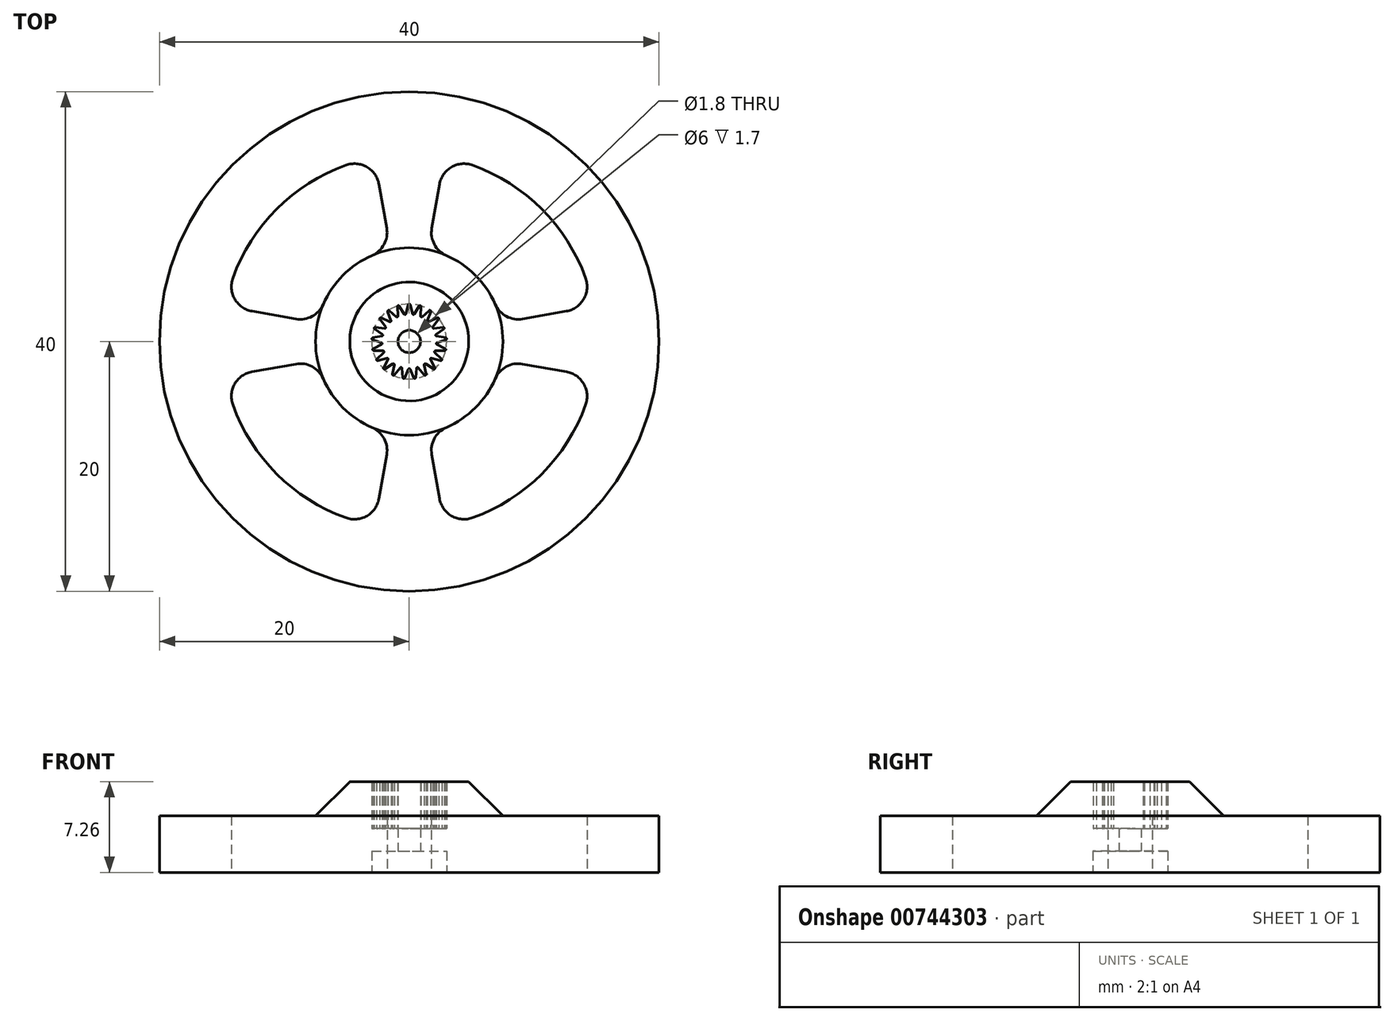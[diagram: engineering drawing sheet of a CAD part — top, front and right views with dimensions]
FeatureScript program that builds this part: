
annotation { "Feature Type Name" : "Feature", "Feature Type Description" : "" }
export const myFeature = defineFeature(function(context is Context, id is Id, definition is map)
    precondition{}
    {
        {
            var Q0;
            Q0=qCreatedBy(makeId("Top.planeOp"),FACE);
            var sketch = newSketch(context, id + "F0", { "sketchPlane" : qUnion([Q0])});
            skCircle(sketch, "E0", {"center": v(0, 0) * mm, "radius": 2.05 * mm, "construction": true});
            skLineSegment(sketch, "E1", {"start": v(-0.26, 2.21) * mm, "end": v(-0.08, 2.94) * mm});
            skLineSegment(sketch, "E2", {"start": v(0.26, 2.21) * mm, "end": v(0.08, 2.94) * mm});
            skArc(sketch, "E3", {"start": v(0.08, 2.94) * mm, "mid": v(0, 3) * mm, "end": v(-0.08, 2.94) * mm});
            skLineSegment(sketch, "E4", {"start": v(-0.3, 2.03) * mm, "end": v(0, 0) * mm, "construction": true});
            skLineSegment(sketch, "E5", {"start": v(0.3, 2.03) * mm, "end": v(0, 0) * mm, "construction": true});
            skLineSegment(sketch, "E6.1.0", {"start": v(-0.9, 2.04) * mm, "end": v(-0.94, 2.79) * mm});
            skArc(sketch, "E6.1.1", {"start": v(-0.8, 2.83) * mm, "mid": v(-0.88, 2.87) * mm, "end": v(-0.94, 2.79) * mm});
            skLineSegment(sketch, "E6.1.2", {"start": v(-0.4, 2.2) * mm, "end": v(-0.8, 2.83) * mm});
            skLineSegment(sketch, "E6.2.0", {"start": v(-1.46, 1.68) * mm, "end": v(-1.72, 2.38) * mm});
            skArc(sketch, "E6.2.1", {"start": v(-1.6, 2.47) * mm, "mid": v(-1.69, 2.48) * mm, "end": v(-1.72, 2.38) * mm});
            skLineSegment(sketch, "E6.2.2", {"start": v(-1.03, 1.97) * mm, "end": v(-1.6, 2.47) * mm});
            skLineSegment(sketch, "E6.3.0", {"start": v(-1.9, 1.18) * mm, "end": v(-2.35, 1.77) * mm});
            skArc(sketch, "E6.3.1", {"start": v(-2.25, 1.9) * mm, "mid": v(-2.35, 1.87) * mm, "end": v(-2.35, 1.77) * mm});
            skLineSegment(sketch, "E6.3.2", {"start": v(-1.57, 1.58) * mm, "end": v(-2.25, 1.9) * mm});
            skLineSegment(sketch, "E6.4.0", {"start": v(-2.16, 0.57) * mm, "end": v(-2.76, 1) * mm});
            skArc(sketch, "E6.4.1", {"start": v(-2.7, 1.15) * mm, "mid": v(-2.8, 1.1) * mm, "end": v(-2.76, 1) * mm});
            skLineSegment(sketch, "E6.4.2", {"start": v(-1.97, 1.05) * mm, "end": v(-2.7, 1.15) * mm});
            skLineSegment(sketch, "E6.5.0", {"start": v(-2.23, -0.1) * mm, "end": v(-2.94, 0.14) * mm});
            skArc(sketch, "E6.5.1", {"start": v(-2.93, 0.3) * mm, "mid": v(-3, 0.22) * mm, "end": v(-2.94, 0.14) * mm});
            skLineSegment(sketch, "E6.5.2", {"start": v(-2.19, 0.42) * mm, "end": v(-2.93, 0.3) * mm});
            skLineSegment(sketch, "E6.6.0", {"start": v(-2.1, -0.75) * mm, "end": v(-2.85, -0.73) * mm});
            skArc(sketch, "E6.6.1", {"start": v(-2.88, -0.58) * mm, "mid": v(-2.92, -0.67) * mm, "end": v(-2.85, -0.73) * mm});
            skLineSegment(sketch, "E6.6.2", {"start": v(-2.22, -0.24) * mm, "end": v(-2.88, -0.58) * mm});
            skLineSegment(sketch, "E6.7.0", {"start": v(-1.79, -1.33) * mm, "end": v(-2.5, -1.54) * mm});
            skArc(sketch, "E6.7.1", {"start": v(-2.58, -1.4) * mm, "mid": v(-2.6, -1.5) * mm, "end": v(-2.5, -1.54) * mm});
            skLineSegment(sketch, "E6.7.2", {"start": v(-2.05, -0.88) * mm, "end": v(-2.58, -1.4) * mm});
            skLineSegment(sketch, "E6.8.0", {"start": v(-1.32, -1.8) * mm, "end": v(-1.94, -2.2) * mm});
            skArc(sketch, "E6.8.1", {"start": v(-2.06, -2.1) * mm, "mid": v(-2.04, -2.2) * mm, "end": v(-1.94, -2.2) * mm});
            skLineSegment(sketch, "E6.8.2", {"start": v(-1.7, -1.45) * mm, "end": v(-2.06, -2.1) * mm});
            skLineSegment(sketch, "E6.9.0", {"start": v(-0.73, -2.1) * mm, "end": v(-1.2, -2.68) * mm});
            skArc(sketch, "E6.9.1", {"start": v(-1.35, -2.61) * mm, "mid": v(-1.3, -2.7) * mm, "end": v(-1.2, -2.68) * mm});
            skLineSegment(sketch, "E6.9.2", {"start": v(-1.2, -1.88) * mm, "end": v(-1.35, -2.61) * mm});
            skLineSegment(sketch, "E6.10.0", {"start": v(-0.07, -2.23) * mm, "end": v(-0.36, -2.92) * mm});
            skArc(sketch, "E6.10.1", {"start": v(-0.51, -2.9) * mm, "mid": v(-0.45, -2.97) * mm, "end": v(-0.36, -2.92) * mm});
            skLineSegment(sketch, "E6.10.2", {"start": v(-0.59, -2.15) * mm, "end": v(-0.51, -2.9) * mm});
            skLineSegment(sketch, "E6.11.0", {"start": v(0.59, -2.15) * mm, "end": v(0.51, -2.9) * mm});
            skArc(sketch, "E6.11.1", {"start": v(0.36, -2.92) * mm, "mid": v(0.45, -2.97) * mm, "end": v(0.51, -2.9) * mm});
            skLineSegment(sketch, "E6.11.2", {"start": v(0.07, -2.23) * mm, "end": v(0.36, -2.92) * mm});
            skLineSegment(sketch, "E6.12.0", {"start": v(1.2, -1.88) * mm, "end": v(1.35, -2.61) * mm});
            skArc(sketch, "E6.12.1", {"start": v(1.2, -2.68) * mm, "mid": v(1.3, -2.7) * mm, "end": v(1.35, -2.61) * mm});
            skLineSegment(sketch, "E6.12.2", {"start": v(0.73, -2.1) * mm, "end": v(1.2, -2.68) * mm});
            skLineSegment(sketch, "E6.13.0", {"start": v(1.7, -1.45) * mm, "end": v(2.06, -2.1) * mm});
            skArc(sketch, "E6.13.1", {"start": v(1.94, -2.2) * mm, "mid": v(2.04, -2.2) * mm, "end": v(2.06, -2.1) * mm});
            skLineSegment(sketch, "E6.13.2", {"start": v(1.32, -1.8) * mm, "end": v(1.94, -2.2) * mm});
            skLineSegment(sketch, "E6.14.0", {"start": v(2.05, -0.88) * mm, "end": v(2.58, -1.4) * mm});
            skArc(sketch, "E6.14.1", {"start": v(2.5, -1.54) * mm, "mid": v(2.6, -1.5) * mm, "end": v(2.58, -1.4) * mm});
            skLineSegment(sketch, "E6.14.2", {"start": v(1.79, -1.33) * mm, "end": v(2.5, -1.54) * mm});
            skLineSegment(sketch, "E6.15.0", {"start": v(2.22, -0.24) * mm, "end": v(2.88, -0.58) * mm});
            skArc(sketch, "E6.15.1", {"start": v(2.85, -0.73) * mm, "mid": v(2.92, -0.67) * mm, "end": v(2.88, -0.58) * mm});
            skLineSegment(sketch, "E6.15.2", {"start": v(2.1, -0.75) * mm, "end": v(2.85, -0.73) * mm});
            skLineSegment(sketch, "E6.16.0", {"start": v(2.19, 0.42) * mm, "end": v(2.93, 0.3) * mm});
            skArc(sketch, "E6.16.1", {"start": v(2.94, 0.14) * mm, "mid": v(3, 0.22) * mm, "end": v(2.93, 0.3) * mm});
            skLineSegment(sketch, "E6.16.2", {"start": v(2.23, -0.1) * mm, "end": v(2.94, 0.14) * mm});
            skLineSegment(sketch, "E6.17.0", {"start": v(1.97, 1.05) * mm, "end": v(2.7, 1.15) * mm});
            skArc(sketch, "E6.17.1", {"start": v(2.76, 1) * mm, "mid": v(2.8, 1.1) * mm, "end": v(2.7, 1.15) * mm});
            skLineSegment(sketch, "E6.17.2", {"start": v(2.16, 0.57) * mm, "end": v(2.76, 1) * mm});
            skLineSegment(sketch, "E6.18.0", {"start": v(1.57, 1.58) * mm, "end": v(2.25, 1.9) * mm});
            skArc(sketch, "E6.18.1", {"start": v(2.35, 1.77) * mm, "mid": v(2.35, 1.87) * mm, "end": v(2.25, 1.9) * mm});
            skLineSegment(sketch, "E6.18.2", {"start": v(1.9, 1.18) * mm, "end": v(2.35, 1.77) * mm});
            skLineSegment(sketch, "E6.19.0", {"start": v(1.03, 1.97) * mm, "end": v(1.6, 2.47) * mm});
            skArc(sketch, "E6.19.1", {"start": v(1.72, 2.38) * mm, "mid": v(1.69, 2.48) * mm, "end": v(1.6, 2.47) * mm});
            skLineSegment(sketch, "E6.19.2", {"start": v(1.46, 1.68) * mm, "end": v(1.72, 2.38) * mm});
            skLineSegment(sketch, "E6.20.0", {"start": v(0.4, 2.2) * mm, "end": v(0.8, 2.83) * mm});
            skArc(sketch, "E6.20.1", {"start": v(0.94, 2.79) * mm, "mid": v(0.88, 2.87) * mm, "end": v(0.8, 2.83) * mm});
            skLineSegment(sketch, "E6.20.2", {"start": v(0.9, 2.04) * mm, "end": v(0.94, 2.79) * mm});
            skCircle(sketch, "E7", {"center": v(0, 0) * mm, "radius": 0.75 * mm, "construction": true});
            skCircle(sketch, "E8", {"center": v(0, 0) * mm, "radius": 4.5 * mm});
            skPoint(sketch, "E9.visualSharp", {"position": v(1.4, 1.5) * mm});
            skArc(sketch, "E9.filletArc", {"start": v(1.46, 1.68) * mm, "mid": v(1.48, 1.6) * mm, "end": v(1.57, 1.58) * mm});
            skPoint(sketch, "E10.visualSharp", {"position": v(0.89, 1.85) * mm});
            skArc(sketch, "E10.filletArc", {"start": v(0.9, 2.04) * mm, "mid": v(0.95, 1.96) * mm, "end": v(1.03, 1.97) * mm});
            skPoint(sketch, "E11.visualSharp", {"position": v(0.3, 2.03) * mm});
            skArc(sketch, "E11.filletArc", {"start": v(0.26, 2.21) * mm, "mid": v(0.32, 2.15) * mm, "end": v(0.4, 2.2) * mm});
            skPoint(sketch, "E12.visualSharp", {"position": v(-0.3, 2.03) * mm});
            skArc(sketch, "E12.filletArc", {"start": v(-0.4, 2.2) * mm, "mid": v(-0.32, 2.15) * mm, "end": v(-0.26, 2.21) * mm});
            skPoint(sketch, "E13.visualSharp", {"position": v(-0.89, 1.85) * mm});
            skArc(sketch, "E13.filletArc", {"start": v(-1.03, 1.97) * mm, "mid": v(-0.95, 1.96) * mm, "end": v(-0.9, 2.04) * mm});
            skPoint(sketch, "E14.visualSharp", {"position": v(-1.4, 1.5) * mm});
            skArc(sketch, "E14.filletArc", {"start": v(-1.57, 1.58) * mm, "mid": v(-1.48, 1.6) * mm, "end": v(-1.46, 1.68) * mm});
            skPoint(sketch, "E15.visualSharp", {"position": v(-1.78, 1.02) * mm});
            skArc(sketch, "E15.filletArc", {"start": v(-1.97, 1.05) * mm, "mid": v(-1.89, 1.09) * mm, "end": v(-1.9, 1.18) * mm});
            skPoint(sketch, "E16.visualSharp", {"position": v(-2, 0.46) * mm});
            skArc(sketch, "E16.filletArc", {"start": v(-2.19, 0.42) * mm, "mid": v(-2.12, 0.48) * mm, "end": v(-2.16, 0.57) * mm});
            skPoint(sketch, "E17.visualSharp", {"position": v(-2.04, -0.15) * mm});
            skArc(sketch, "E17.filletArc", {"start": v(-2.22, -0.24) * mm, "mid": v(-2.17, -0.16) * mm, "end": v(-2.23, -0.1) * mm});
            skPoint(sketch, "E18.visualSharp", {"position": v(-1.9, -0.75) * mm});
            skArc(sketch, "E18.filletArc", {"start": v(-2.05, -0.88) * mm, "mid": v(-2.03, -0.8) * mm, "end": v(-2.1, -0.75) * mm});
            skPoint(sketch, "E19.visualSharp", {"position": v(-1.6, -1.28) * mm});
            skArc(sketch, "E19.filletArc", {"start": v(-1.7, -1.45) * mm, "mid": v(-1.7, -1.36) * mm, "end": v(-1.79, -1.33) * mm});
            skPoint(sketch, "E20.visualSharp", {"position": v(-1.15, -1.7) * mm});
            skArc(sketch, "E20.filletArc", {"start": v(-1.2, -1.88) * mm, "mid": v(-1.23, -1.8) * mm, "end": v(-1.32, -1.8) * mm});
            skPoint(sketch, "E21.visualSharp", {"position": v(-0.6, -1.96) * mm});
            skArc(sketch, "E21.filletArc", {"start": v(-0.59, -2.15) * mm, "mid": v(-0.64, -2.08) * mm, "end": v(-0.73, -2.1) * mm});
            skPoint(sketch, "E22.visualSharp", {"position": v(0, -2.05) * mm});
            skArc(sketch, "E22.filletArc", {"start": v(0.07, -2.23) * mm, "mid": v(0, -2.18) * mm, "end": v(-0.07, -2.23) * mm});
            skPoint(sketch, "E23.visualSharp", {"position": v(0.6, -1.96) * mm});
            skArc(sketch, "E23.filletArc", {"start": v(0.73, -2.1) * mm, "mid": v(0.64, -2.08) * mm, "end": v(0.59, -2.15) * mm});
            skPoint(sketch, "E24.visualSharp", {"position": v(1.15, -1.7) * mm});
            skArc(sketch, "E24.filletArc", {"start": v(1.32, -1.8) * mm, "mid": v(1.23, -1.8) * mm, "end": v(1.2, -1.88) * mm});
            skPoint(sketch, "E25.visualSharp", {"position": v(1.9, -0.75) * mm});
            skArc(sketch, "E25.filletArc", {"start": v(2.1, -0.75) * mm, "mid": v(2.03, -0.8) * mm, "end": v(2.05, -0.88) * mm});
            skPoint(sketch, "E26.visualSharp", {"position": v(1.6, -1.28) * mm});
            skArc(sketch, "E26.filletArc", {"start": v(1.79, -1.33) * mm, "mid": v(1.7, -1.36) * mm, "end": v(1.7, -1.45) * mm});
            skPoint(sketch, "E27.visualSharp", {"position": v(2.04, -0.15) * mm});
            skArc(sketch, "E27.filletArc", {"start": v(2.23, -0.1) * mm, "mid": v(2.17, -0.16) * mm, "end": v(2.22, -0.24) * mm});
            skPoint(sketch, "E28.visualSharp", {"position": v(2, 0.46) * mm});
            skArc(sketch, "E28.filletArc", {"start": v(2.16, 0.57) * mm, "mid": v(2.12, 0.48) * mm, "end": v(2.19, 0.42) * mm});
            skPoint(sketch, "E29.visualSharp", {"position": v(1.78, 1.02) * mm});
            skArc(sketch, "E29.filletArc", {"start": v(1.9, 1.18) * mm, "mid": v(1.89, 1.09) * mm, "end": v(1.97, 1.05) * mm});
            skSolve(sketch);
        }
        {
            var Q0;
            Q0 = qSketchRegion(id + "F0", true);
            extrude(context, id + "F1", {"entities" : qUnion([Q0]), "depth" : 5 * mm, "offsetDistance" : 25 * mm});
        }
        {
            var Q0;
            Q0=qCreatedBy(makeId("Top.planeOp"),FACE);
            var sketch = newSketch(context, id + "F2", { "sketchPlane" : qUnion([Q0])});
            skCircle(sketch, "E30", {"center": v(0, 0) * mm, "radius": 20 * mm});
            skCircle(sketch, "E31", {"center": v(0, 0) * mm, "radius": 0.9 * mm});
            skArc(sketch, "E32", {"start": v(6.88, 2.98) * mm, "mid": v(5.3, 5.3) * mm, "end": v(2.98, 6.88) * mm});
            skArc(sketch, "E33", {"start": v(14.12, 5.07) * mm, "mid": v(10.6, 10.6) * mm, "end": v(5.07, 14.12) * mm});
            skLineSegment(sketch, "E34.trimOffspring", {"start": v(9.07, 1.8) * mm, "end": v(12.58, 2.42) * mm});
            skLineSegment(sketch, "E35.trimOffspring", {"start": v(1.8, 9.07) * mm, "end": v(2.42, 12.58) * mm});
            skPoint(sketch, "E36.visualSharp", {"position": v(14.74, 2.8) * mm});
            skArc(sketch, "E36.filletArc", {"start": v(12.58, 2.42) * mm, "mid": v(13.97, 3.39) * mm, "end": v(14.12, 5.07) * mm});
            skPoint(sketch, "E37.visualSharp", {"position": v(7.35, 1.5) * mm});
            skArc(sketch, "E37.filletArc", {"start": v(6.88, 2.98) * mm, "mid": v(7.77, 2.01) * mm, "end": v(9.07, 1.8) * mm});
            skPoint(sketch, "E38.visualSharp", {"position": v(1.5, 7.35) * mm});
            skArc(sketch, "E38.filletArc", {"start": v(1.8, 9.07) * mm, "mid": v(2.01, 7.77) * mm, "end": v(2.98, 6.88) * mm});
            skPoint(sketch, "E39.visualSharp", {"position": v(2.8, 14.74) * mm});
            skArc(sketch, "E39.filletArc", {"start": v(5.07, 14.12) * mm, "mid": v(3.39, 13.97) * mm, "end": v(2.42, 12.58) * mm});
            skArc(sketch, "E40.MirrorCS", {"start": v(-6.88, 2.98) * mm, "mid": v(-7.77, 2.01) * mm, "end": v(-9.07, 1.8) * mm});
            skArc(sketch, "E41.MirrorCS", {"start": v(-6.88, 2.98) * mm, "mid": v(-5.3, 5.3) * mm, "end": v(-2.98, 6.88) * mm});
            skArc(sketch, "E42.MirrorCS", {"start": v(-1.8, 9.07) * mm, "mid": v(-2.01, 7.77) * mm, "end": v(-2.98, 6.88) * mm});
            skLineSegment(sketch, "E43.MirrorCS", {"start": v(-9.07, 1.8) * mm, "end": v(-12.58, 2.42) * mm});
            skLineSegment(sketch, "E44.MirrorCS", {"start": v(-1.8, 9.07) * mm, "end": v(-2.42, 12.58) * mm});
            skArc(sketch, "E45.MirrorCS", {"start": v(-5.07, 14.12) * mm, "mid": v(-3.39, 13.97) * mm, "end": v(-2.42, 12.58) * mm});
            skArc(sketch, "E46.MirrorCS", {"start": v(-14.12, 5.07) * mm, "mid": v(-10.6, 10.6) * mm, "end": v(-5.07, 14.12) * mm});
            skArc(sketch, "E47.MirrorCS", {"start": v(-12.58, 2.42) * mm, "mid": v(-13.97, 3.39) * mm, "end": v(-14.12, 5.07) * mm});
            skArc(sketch, "E48.MirrorCS", {"start": v(1.8, -9.07) * mm, "mid": v(2.01, -7.77) * mm, "end": v(2.98, -6.88) * mm});
            skArc(sketch, "E49.MirrorCS", {"start": v(6.88, -2.98) * mm, "mid": v(5.3, -5.3) * mm, "end": v(2.98, -6.88) * mm});
            skArc(sketch, "E50.MirrorCS", {"start": v(6.88, -2.98) * mm, "mid": v(7.77, -2.01) * mm, "end": v(9.07, -1.8) * mm});
            skLineSegment(sketch, "E51.MirrorCS", {"start": v(9.07, -1.8) * mm, "end": v(12.58, -2.42) * mm});
            skArc(sketch, "E52.MirrorCS", {"start": v(12.58, -2.42) * mm, "mid": v(13.97, -3.39) * mm, "end": v(14.12, -5.07) * mm});
            skArc(sketch, "E53.MirrorCS", {"start": v(14.12, -5.07) * mm, "mid": v(10.6, -10.6) * mm, "end": v(5.07, -14.12) * mm});
            skArc(sketch, "E54.MirrorCS", {"start": v(5.07, -14.12) * mm, "mid": v(3.39, -13.97) * mm, "end": v(2.42, -12.58) * mm});
            skLineSegment(sketch, "E55.MirrorCS", {"start": v(1.8, -9.07) * mm, "end": v(2.42, -12.58) * mm});
            skArc(sketch, "E56.MirrorCS", {"start": v(-5.07, -14.12) * mm, "mid": v(-3.39, -13.97) * mm, "end": v(-2.42, -12.58) * mm});
            skLineSegment(sketch, "E57.MirrorCS", {"start": v(-9.07, -1.8) * mm, "end": v(-12.58, -2.42) * mm});
            skLineSegment(sketch, "E58.MirrorCS", {"start": v(-1.8, -9.07) * mm, "end": v(-2.42, -12.58) * mm});
            skArc(sketch, "E59.MirrorCS", {"start": v(-1.8, -9.07) * mm, "mid": v(-2.01, -7.77) * mm, "end": v(-2.98, -6.88) * mm});
            skArc(sketch, "E60.MirrorCS", {"start": v(-6.88, -2.98) * mm, "mid": v(-5.3, -5.3) * mm, "end": v(-2.98, -6.88) * mm});
            skArc(sketch, "E61.MirrorCS", {"start": v(-6.88, -2.98) * mm, "mid": v(-7.77, -2.01) * mm, "end": v(-9.07, -1.8) * mm});
            skArc(sketch, "E62.MirrorCS", {"start": v(-12.58, -2.42) * mm, "mid": v(-13.97, -3.39) * mm, "end": v(-14.12, -5.07) * mm});
            skArc(sketch, "E63.MirrorCS", {"start": v(-14.12, -5.07) * mm, "mid": v(-10.6, -10.6) * mm, "end": v(-5.07, -14.12) * mm});
            skSolve(sketch);
        }
        {
            var Q0;
            Q0 = qSketchRegion(id + "F2", true);
            extrude(context, id + "F3", {"entities" : qUnion([Q0]), "operationType" : NewBodyOperationType.ADD, "endBound" : BoundingType.SYMMETRIC, "depth" : 4.52 * mm, "offsetDistance" : 25 * mm});
        }
        {
            var Q0;
            Q0=makeQuery(id+"F3.opExtrude","CAP_FACE",FACE,{"disambiguationData":[OSD([sQuery(id+"F2.wireOp",EDGE,"E30"),sQuery(id+"F2.wireOp",EDGE,"E31"),sQuery(id+"F2.wireOp",EDGE,"E32"),sQuery(id+"F2.wireOp",EDGE,"E33"),sQuery(id+"F2.wireOp",EDGE,"E34.trimOffspring"),sQuery(id+"F2.wireOp",EDGE,"E35.trimOffspring"),sQuery(id+"F2.wireOp",EDGE,"E36.filletArc"),sQuery(id+"F2.wireOp",EDGE,"E37.filletArc"),sQuery(id+"F2.wireOp",EDGE,"E38.filletArc"),sQuery(id+"F2.wireOp",EDGE,"E39.filletArc"),sQuery(id+"F2.wireOp",EDGE,"E40.MirrorCS"),sQuery(id+"F2.wireOp",EDGE,"E41.MirrorCS"),sQuery(id+"F2.wireOp",EDGE,"E42.MirrorCS"),sQuery(id+"F2.wireOp",EDGE,"E43.MirrorCS"),sQuery(id+"F2.wireOp",EDGE,"E44.MirrorCS"),sQuery(id+"F2.wireOp",EDGE,"E45.MirrorCS"),sQuery(id+"F2.wireOp",EDGE,"E46.MirrorCS"),sQuery(id+"F2.wireOp",EDGE,"E47.MirrorCS"),sQuery(id+"F2.wireOp",EDGE,"E48.MirrorCS"),sQuery(id+"F2.wireOp",EDGE,"E49.MirrorCS"),sQuery(id+"F2.wireOp",EDGE,"E50.MirrorCS"),sQuery(id+"F2.wireOp",EDGE,"E51.MirrorCS"),sQuery(id+"F2.wireOp",EDGE,"E52.MirrorCS"),sQuery(id+"F2.wireOp",EDGE,"E53.MirrorCS"),sQuery(id+"F2.wireOp",EDGE,"E54.MirrorCS"),sQuery(id+"F2.wireOp",EDGE,"E55.MirrorCS"),sQuery(id+"F2.wireOp",EDGE,"E56.MirrorCS"),sQuery(id+"F2.wireOp",EDGE,"E57.MirrorCS"),sQuery(id+"F2.wireOp",EDGE,"E58.MirrorCS"),sQuery(id+"F2.wireOp",EDGE,"E59.MirrorCS"),sQuery(id+"F2.wireOp",EDGE,"E60.MirrorCS"),sQuery(id+"F2.wireOp",EDGE,"E61.MirrorCS"),sQuery(id+"F2.wireOp",EDGE,"E62.MirrorCS"),sQuery(id+"F2.wireOp",EDGE,"E63.MirrorCS")])],"isStart":true});
            var sketch = newSketch(context, id + "F4", { "sketchPlane" : qUnion([Q0])});
            skCircle(sketch, "E64", {"center": v(0, 0) * mm, "radius": 3 * mm});
            skSolve(sketch);
        }
        {
            var Q0;
            Q0 = qSketchRegion(id + "F4", true);
            extrude(context, id + "F5", {"entities" : qUnion([Q0]), "operationType" : NewBodyOperationType.REMOVE, "oppositeDirection" : true, "depth" : 1.7 * mm, "offsetDistance" : 25 * mm});
        }
        {
            var Q0;
            Q0=qCreatedBy(makeId("Front.planeOp"),FACE);
            var sketch = newSketch(context, id + "F6", { "sketchPlane" : qUnion([Q0])});
            skCircle(sketch, "E65", {"center": v(-13.75, 0) * mm, "radius": 1.5 * mm});
            skLineSegment(sketch, "E66", {"start": v(0, 9.3) * mm, "end": v(0, -10.77) * mm, "construction": true});
            skSolve(sketch);
        }
        {
            var Q0;
            Q0=makeQuery(id+"F3.boolean.opBoolean","INTERSECT",EDGE,{"derivedFrom":[makeQuery(id+"F1.opExtrude","SWEPT_FACE",FACE,{"disambiguationData":[OSD([sQuery(id+"F0.wireOp",EDGE,"E8")])]}),makeQuery(id+"F3.opExtrude","CAP_FACE",FACE,{"disambiguationData":[OSD([sQuery(id+"F2.wireOp",EDGE,"E30"),sQuery(id+"F2.wireOp",EDGE,"E31"),sQuery(id+"F2.wireOp",EDGE,"E32"),sQuery(id+"F2.wireOp",EDGE,"E33"),sQuery(id+"F2.wireOp",EDGE,"E34.trimOffspring"),sQuery(id+"F2.wireOp",EDGE,"E35.trimOffspring"),sQuery(id+"F2.wireOp",EDGE,"E36.filletArc"),sQuery(id+"F2.wireOp",EDGE,"E37.filletArc"),sQuery(id+"F2.wireOp",EDGE,"E38.filletArc"),sQuery(id+"F2.wireOp",EDGE,"E39.filletArc"),sQuery(id+"F2.wireOp",EDGE,"E40.MirrorCS"),sQuery(id+"F2.wireOp",EDGE,"E41.MirrorCS"),sQuery(id+"F2.wireOp",EDGE,"E42.MirrorCS"),sQuery(id+"F2.wireOp",EDGE,"E43.MirrorCS"),sQuery(id+"F2.wireOp",EDGE,"E44.MirrorCS"),sQuery(id+"F2.wireOp",EDGE,"E45.MirrorCS"),sQuery(id+"F2.wireOp",EDGE,"E46.MirrorCS"),sQuery(id+"F2.wireOp",EDGE,"E47.MirrorCS"),sQuery(id+"F2.wireOp",EDGE,"E48.MirrorCS"),sQuery(id+"F2.wireOp",EDGE,"E49.MirrorCS"),sQuery(id+"F2.wireOp",EDGE,"E50.MirrorCS"),sQuery(id+"F2.wireOp",EDGE,"E51.MirrorCS"),sQuery(id+"F2.wireOp",EDGE,"E52.MirrorCS"),sQuery(id+"F2.wireOp",EDGE,"E53.MirrorCS"),sQuery(id+"F2.wireOp",EDGE,"E54.MirrorCS"),sQuery(id+"F2.wireOp",EDGE,"E55.MirrorCS"),sQuery(id+"F2.wireOp",EDGE,"E56.MirrorCS"),sQuery(id+"F2.wireOp",EDGE,"E57.MirrorCS"),sQuery(id+"F2.wireOp",EDGE,"E58.MirrorCS"),sQuery(id+"F2.wireOp",EDGE,"E59.MirrorCS"),sQuery(id+"F2.wireOp",EDGE,"E60.MirrorCS"),sQuery(id+"F2.wireOp",EDGE,"E61.MirrorCS"),sQuery(id+"F2.wireOp",EDGE,"E62.MirrorCS"),sQuery(id+"F2.wireOp",EDGE,"E63.MirrorCS")])],"isStart":false})]});
            chamfer(context, id + "F7", {"entities" : qUnion([Q0]), "width" : 3 * mm, "tangentPropagation" : true});
        }
        {
            var Q0;
            {var subQ0=sQuery(id+"F2.wireOp",EDGE,"E31");Q0=makeQuery(id+"F3.boolean.opBoolean","SPLIT",FACE,{"disambiguationData":[TD([makeQuery(id+"F1.opExtrude","SWEPT_FACE",FACE,{"disambiguationData":[OSD([sQuery(id+"F0.wireOp",EDGE,"E1")])]})])],"derivedFrom":makeQuery(id+"F3.opExtrude","CAP_FACE",FACE,{"disambiguationData":[OSD([sQuery(id+"F2.wireOp",EDGE,"E30"),subQ0,sQuery(id+"F2.wireOp",EDGE,"E32"),sQuery(id+"F2.wireOp",EDGE,"E33"),sQuery(id+"F2.wireOp",EDGE,"E34.trimOffspring"),sQuery(id+"F2.wireOp",EDGE,"E35.trimOffspring"),sQuery(id+"F2.wireOp",EDGE,"E36.filletArc"),sQuery(id+"F2.wireOp",EDGE,"E37.filletArc"),sQuery(id+"F2.wireOp",EDGE,"E38.filletArc"),sQuery(id+"F2.wireOp",EDGE,"E39.filletArc"),sQuery(id+"F2.wireOp",EDGE,"E40.MirrorCS"),sQuery(id+"F2.wireOp",EDGE,"E41.MirrorCS"),sQuery(id+"F2.wireOp",EDGE,"E42.MirrorCS"),sQuery(id+"F2.wireOp",EDGE,"E43.MirrorCS"),sQuery(id+"F2.wireOp",EDGE,"E44.MirrorCS"),sQuery(id+"F2.wireOp",EDGE,"E45.MirrorCS"),sQuery(id+"F2.wireOp",EDGE,"E46.MirrorCS"),sQuery(id+"F2.wireOp",EDGE,"E47.MirrorCS"),sQuery(id+"F2.wireOp",EDGE,"E48.MirrorCS"),sQuery(id+"F2.wireOp",EDGE,"E49.MirrorCS"),sQuery(id+"F2.wireOp",EDGE,"E50.MirrorCS"),sQuery(id+"F2.wireOp",EDGE,"E51.MirrorCS"),sQuery(id+"F2.wireOp",EDGE,"E52.MirrorCS"),sQuery(id+"F2.wireOp",EDGE,"E53.MirrorCS"),sQuery(id+"F2.wireOp",EDGE,"E54.MirrorCS"),sQuery(id+"F2.wireOp",EDGE,"E55.MirrorCS"),sQuery(id+"F2.wireOp",EDGE,"E56.MirrorCS"),sQuery(id+"F2.wireOp",EDGE,"E57.MirrorCS"),sQuery(id+"F2.wireOp",EDGE,"E58.MirrorCS"),sQuery(id+"F2.wireOp",EDGE,"E59.MirrorCS"),sQuery(id+"F2.wireOp",EDGE,"E60.MirrorCS"),sQuery(id+"F2.wireOp",EDGE,"E61.MirrorCS"),sQuery(id+"F2.wireOp",EDGE,"E62.MirrorCS"),sQuery(id+"F2.wireOp",EDGE,"E63.MirrorCS")])],"isStart":false})});}
            extrude(context, id + "F8", {"entities" : qUnion([Q0]), "operationType" : NewBodyOperationType.REMOVE, "oppositeDirection" : true, "depth" : 1 * mm, "offsetDistance" : 25 * mm});
        }
    });
